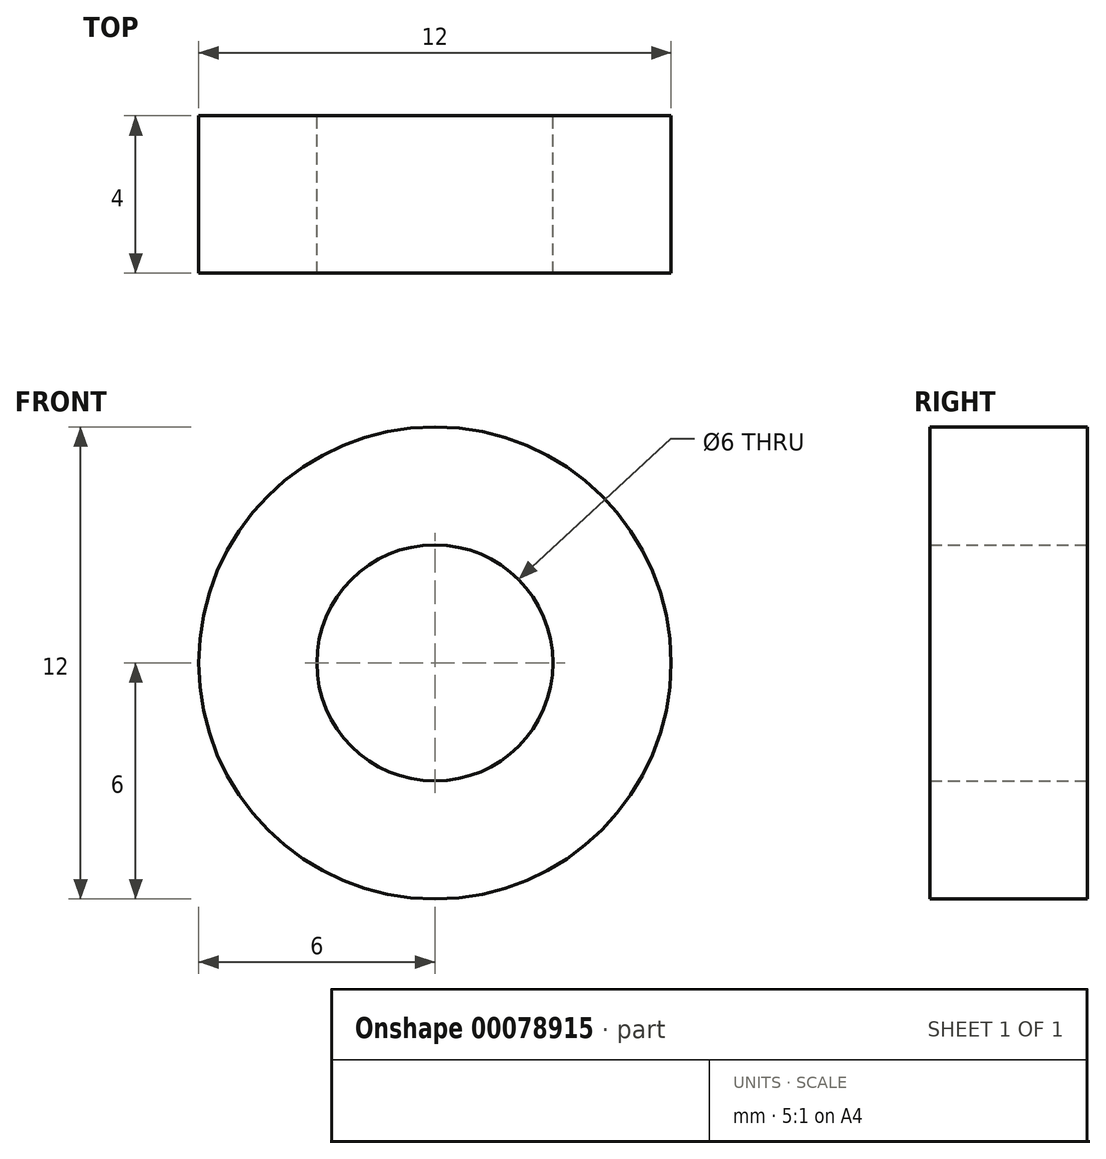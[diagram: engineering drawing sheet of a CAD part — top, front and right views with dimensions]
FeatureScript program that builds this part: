
annotation { "Feature Type Name" : "Feature", "Feature Type Description" : "" }
export const myFeature = defineFeature(function(context is Context, id is Id, definition is map)
    precondition{}
    {
        {
            var Q0;
            Q0=qCreatedBy(makeId("Front.planeOp"),FACE);
            var sketch = newSketch(context, id + "F0", { "sketchPlane" : qUnion([Q0])});
            skCircle(sketch, "E0", {"center": v(0, 0) * mm, "radius": 3 * mm});
            skCircle(sketch, "E1", {"center": v(0, 0) * mm, "radius": 6 * mm});
            skSolve(sketch);
        }
        {
            var Q0;
            Q0 = qSketchRegion(id + "F0", true);
            extrude(context, id + "F1", {"entities" : qUnion([Q0]), "depth" : 4 * mm});
        }
    });
